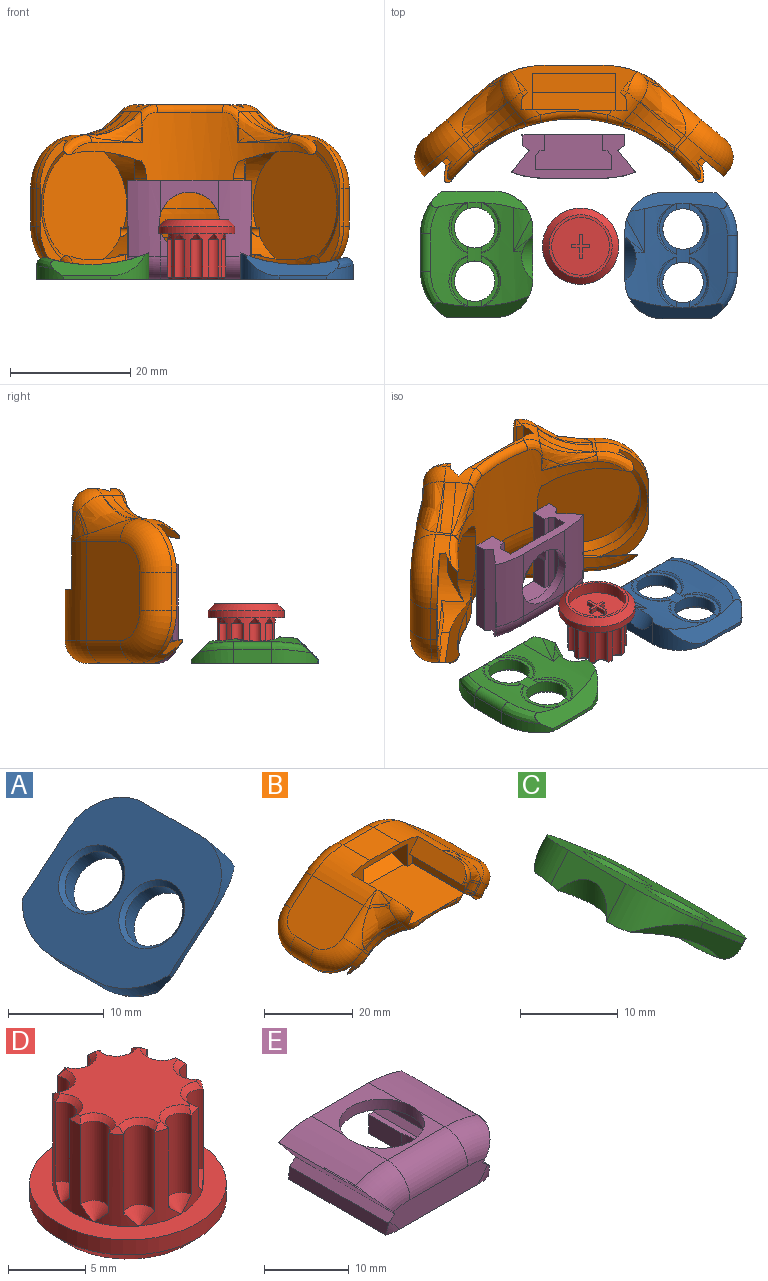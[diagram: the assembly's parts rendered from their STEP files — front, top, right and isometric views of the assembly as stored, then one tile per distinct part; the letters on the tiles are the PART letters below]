
ASSEMBLY  parts=5 mates=4
PART A: 33 faces, bbox 21.6x22.9x17.5 mm
  f0: torus R=39.28mm, axis (0,1,0), area 1.7mm2, adj f1,f2,f26,f30
  f1: cylinder r=25.31mm len=17.23mm, axis (0,1,0), area 130.5mm2, adj f0,f3,f4,f5,f7,f8,f9,f12
  f2: plane 8.4x3.45mm, normal (0.77,0,0.64), area 21.4mm2, adj f0,f23,f26,f28,f29,f30
  f3: cylinder r=1.27mm len=6.27mm, axis (0,1,0), area 14.9mm2, adj f1,f9,f11,f15
  f4: bspline ~8.68x3.45mm, area 3.7mm2, adj f1,f5,f25
  f5: plane 8.42x2.16mm, normal (0.64,0,-0.77), area 6.4mm2, adj f1,f4,f6,f13,f25
  f6: cylinder r=25.31mm len=1.74mm, axis (0,1,0), area 2.3mm2, adj f5,f7,f13,f25
  f7: plane 8.41x2.15mm, normal (0.64,0,-0.77), area 6.4mm2, adj f1,f6,f8,f13,f25
  f8: bspline ~8.68x3.09mm, area 3.7mm2, adj f1,f7,f25
  f9: bspline ~9.49x4.39mm, area 15.5mm2, adj f1,f3,f10,f25
  f10: cylinder r=8.89mm len=7.68mm, axis (0.64,0,-0.77), area 17.4mm2, adj f9,f11,f23,f24,f25
  f11: plane 6.27x1.82mm, normal (-0.77,0,-0.64), area 14.9mm2, adj f3,f10,f14,f23
  f12: cylinder r=3.37mm len=6.73mm, axis (0.64,0,-0.77), area 42.4mm2, adj f1,f17,f18,f19,f32
  f13: cylinder r=3.37mm len=6.73mm, axis (0.64,0,-0.77), area 42.4mm2, adj f1,f5,f6,f7,f31
  f14: cylinder r=8.89mm len=7.09mm, axis (0.64,0,-0.77), area 15.8mm2, adj f11,f15,f21,f22,f23
  f15: bspline ~9.03x3.89mm, area 13.3mm2, adj f1,f3,f14,f21
  f16: bspline ~8.68x3.09mm, area 3.7mm2, adj f1,f17,f21
  f17: plane 8.42x2.16mm, normal (0.64,0,-0.77), area 6.4mm2, adj f1,f12,f16,f18,f21
  f18: cylinder r=25.31mm len=1.74mm, axis (0,1,0), area 2.3mm2, adj f12,f17,f19,f21
  f19: plane 8.41x2.15mm, normal (0.64,0,-0.77), area 6.4mm2, adj f1,f12,f18,f20,f21
  f20: bspline ~8.68x3.45mm, area 3.7mm2, adj f1,f19,f21
  f21: plane 14.76x11.65mm, normal (0.45,0.71,-0.54), area 42.6mm2, adj f1,f14,f15,f16,f17,f18,f19,f20
  f22: plane 7.16x6.15mm, normal (0,1,0), area 5.5mm2, adj f14,f21,f23,f29
  f23: plane 21.03x14.32mm, normal (-0.64,0,0.77), area 264.2mm2, adj f2,f10,f11,f14,f22,f24,f28,f29
  f24: plane 6.48x5.58mm, normal (0,-1,0), area 4.9mm2, adj f10,f23,f25,f28
  f25: plane 15.01x11.45mm, normal (0.45,-0.71,-0.54), area 40.6mm2, adj f1,f4,f5,f6,f7,f8,f9,f10
  f26: bspline ~7.32x5.84mm, area 4.3mm2, adj f0,f2,f27,f29
  f27: cylinder r=13.97mm len=7.35mm, axis (0,1,0), area 12.5mm2, adj f1,f21,f26,f29
  f28: cylinder r=6.35mm len=7.7mm, axis (-0.64,0,0.77), area 25.5mm2, adj f1,f2,f23,f24,f25
  f29: cylinder r=6.35mm len=7.4mm, axis (0.64,0,-0.77), area 24.1mm2, adj f2,f21,f22,f23,f26,f27
  f30: cylinder r=4.57mm len=7.23mm, axis (0,0,-1), area 14.8mm2, adj f0,f1,f2
  f31: cone r=3.87mm half-angle=45deg, axis (-0.64,0,0.77), area 16.3mm2, adj f13,f23
  f32: cone r=3.87mm half-angle=45deg, axis (-0.64,0,0.77), area 16.3mm2, adj f12,f23
PART B: 137 faces, bbox 56.1x34.6x24.1 mm
  f0: plane 21.12x7.53mm, normal (0,-1,0), area 47.6mm2, adj f1,f2,f3,f99,f100,f101,f102,f103
  f1: cylinder r=15.24mm len=16.43mm, axis (0,1,0), area 128.4mm2, adj f0,f2,f10,f42,f77,f106
  f2: plane 9.64x8.55mm, normal (0,0,1), area 82.4mm2, adj f0,f1,f3,f76
  f3: cylinder r=15.24mm len=16.43mm, axis (0,1,0), area 128.4mm2, adj f0,f2,f41,f70,f74,f99
  f4: plane 12.68x0.82mm, normal (0,-1,0), area 4.9mm2, adj f7,f62,f72,f102
  f5: plane 1.14x0.86mm, normal (0,-1,0), area 0.5mm2, adj f7,f80,f105,f106
  f6: torus R=11.43mm, axis (0,-1,0), area 1.4mm2, adj f50,f75,f99
  f7: cylinder r=3.81mm len=5.54mm, axis (-0.64,0,-0.77), area 10.3mm2, adj f4,f5,f8,f78,f102,f103,f104,f105
  f8: sphere r=3.81mm, area 17.1mm2, adj f7,f9,f80,f106,f128,f129,f130
  f9: cylinder r=3.81mm len=3.91mm, axis (0,1,0), area 2.8mm2, adj f8,f106,f131
  f10: torus R=11.43mm, axis (0,1,0), area 3.6mm2, adj f1,f84,f106,f130,f131
  f11: cylinder r=25.31mm len=39.45mm, axis (0,1,0), area 308.2mm2, adj f13,f19,f24,f36,f38,f60,f61,f62
  f12: cylinder r=13.97mm len=4.51mm, axis (0,1,0), area 15.7mm2, adj f15,f25,f30,f45,f53,f96
  f13: torus R=39.28mm, axis (0,1,0), area 71.2mm2, adj f11,f15,f16,f43,f85,f86
  f14: cylinder r=13.97mm len=4.51mm, axis (0,1,0), area 15.7mm2, adj f16,f20,f29,f47,f58,f98
  f15: bspline ~7.09x5.93mm, area 4.8mm2, adj f12,f13,f45,f86,f96
  f16: bspline ~7.09x5.93mm, area 4.8mm2, adj f13,f14,f47,f85,f98
  f17: plane 21.59x6.29mm, normal (-0.64,0,-0.77), area 31.4mm2, adj f18,f21,f27,f32,f34,f133
  f18: plane 7.19x6.61mm, normal (0,1,0), area 9.2mm2, adj f17,f19,f34,f97,f133
  f19: plane 15.28x11.48mm, normal (0.45,0.71,0.54), area 38.4mm2, adj f11,f18,f34,f38,f97
  f20: plane 14.87x11.66mm, normal (0.45,-0.71,0.54), area 40.3mm2, adj f14,f21,f29,f32,f37,f98
  f21: plane 7.96x7.26mm, normal (0,-1,0), area 10.2mm2, adj f17,f20,f32,f98,f133
  f22: plane 21.59x6.29mm, normal (0.64,0,-0.77), area 31.4mm2, adj f23,f26,f28,f31,f33,f132
  f23: plane 7.19x6.61mm, normal (0,1,0), area 9.2mm2, adj f22,f24,f33,f95,f132
  f24: plane 15.28x11.48mm, normal (-0.45,0.71,0.54), area 38.4mm2, adj f11,f23,f33,f36,f95
  f25: plane 14.88x11.66mm, normal (-0.45,-0.71,0.54), area 40.3mm2, adj f12,f26,f30,f31,f35,f96
  f26: plane 7.96x7.26mm, normal (0,-1,0), area 10.2mm2, adj f22,f25,f31,f96,f132
  f27: plane 6.27x0.78mm, normal (0.77,0,-0.64), area 6.4mm2, adj f17,f32,f34,f82
  f28: plane 6.27x0.78mm, normal (-0.77,0,-0.64), area 6.4mm2, adj f22,f31,f33,f66
  f29: cylinder r=25.31mm len=9.36mm, axis (0,1,0), area 26mm2, adj f14,f20,f37,f59
  f30: cylinder r=25.31mm len=9.36mm, axis (0,1,0), area 26mm2, adj f12,f25,f35,f55
  f31: cylinder r=8.89mm len=8.89mm, axis (0.64,0,-0.77), area 24mm2, adj f22,f25,f26,f28,f35,f49,f68
  f32: cylinder r=8.89mm len=8.89mm, axis (0.64,0,0.77), area 24mm2, adj f17,f20,f21,f27,f37,f49,f81
  f33: cylinder r=8.89mm len=8.89mm, axis (0.64,0,-0.77), area 21.7mm2, adj f22,f23,f24,f28,f36,f40,f65
  f34: cylinder r=8.89mm len=8.89mm, axis (0.64,0,0.77), area 21.7mm2, adj f17,f18,f19,f27,f38,f39,f83
  f35: bspline ~7.63x7.4mm, area 14mm2, adj f25,f30,f31,f55
  f36: bspline ~7.2x7.09mm, area 13.2mm2, adj f11,f24,f33,f60
  f37: bspline ~7.97x7.63mm, area 14.1mm2, adj f20,f29,f32,f59
  f38: bspline ~7.63x7.4mm, area 13.2mm2, adj f11,f19,f34,f64
  f39: plane 2.3x2.04mm, normal (0,-1,0), area 1.4mm2, adj f34,f64,f84,f127,f128
  f40: plane 2.3x2.04mm, normal (0,-1,0), area 1.4mm2, adj f33,f60,f67,f119,f120
  f41: plane 16.43x10.53mm, normal (-0.64,0,0.77), area 214.6mm2, adj f3,f65,f66,f67,f68,f71
  f42: plane 16.43x10.53mm, normal (0.64,0,0.77), area 214.6mm2, adj f1,f79,f81,f82,f83,f84
  f43: cone r=29.12mm half-angle=20.6deg, axis (0,1,0), area 46.9mm2, adj f13,f44,f45,f47
  f44: torus R=15.15mm, axis (0,-1,0), area 3.3mm2, adj f43,f46,f48,f54
  f45: bspline ~10.91x6.7mm, area 21.1mm2, adj f12,f15,f43,f46,f51
  f46: bspline ~5.27x4.34mm, area 0.5mm2, adj f44,f45,f52
  f47: bspline ~9.02x6.04mm, area 21.1mm2, adj f14,f16,f43,f48,f57
  f48: bspline ~4.48x4.13mm, area 0.5mm2, adj f44,f47,f56
  f49: plane 37.6x10.17mm, normal (0,1,0), area 101.9mm2, adj f31,f32,f51,f52,f53,f54,f55,f56
  f50: plane 1.14x0.86mm, normal (0,-1,0), area 0.5mm2, adj f6,f72,f99,f100
  f51: bspline ~4.66x4.28mm, area 6mm2, adj f45,f49,f52,f53
  f52: bspline ~4.9x2.39mm, area 3mm2, adj f46,f49,f51,f54
  f53: torus R=12.7mm, axis (0,-1,0), area 10.6mm2, adj f12,f49,f51,f55
  f54: torus R=29.67mm, axis (0,-1,0), area 7.7mm2, adj f44,f49,f52,f56
  f55: torus R=26.58mm, axis (0,-1,0), area 13.5mm2, adj f30,f35,f49,f53
  f56: bspline ~5.22x2.59mm, area 3mm2, adj f48,f49,f54,f57
  f57: bspline ~4.76x4mm, area 6mm2, adj f47,f49,f56,f58
  f58: torus R=12.7mm, axis (0,-1,0), area 10.6mm2, adj f14,f49,f57,f59
  f59: torus R=26.58mm, axis (0,-1,0), area 13.5mm2, adj f29,f37,f49,f58
  f60: torus R=26.58mm, axis (0,1,0), area 4.1mm2, adj f11,f36,f40,f116,f117,f118
  f61: cylinder r=1.27mm len=2.54mm, axis (0,1,0), area 0.2mm2, adj f11,f69,f116
  f62: torus R=26.58mm, axis (0,-1,0), area 22.1mm2, adj f4,f11,f69,f78
  f63: cylinder r=1.27mm len=2.54mm, axis (0,1,0), area 0.2mm2, adj f11,f78,f124
  f64: torus R=26.58mm, axis (0,1,0), area 4.1mm2, adj f11,f38,f39,f124,f125,f126
  f65: torus R=5.08mm, axis (0.64,0,-0.77), area 70.6mm2, adj f33,f41,f66,f67
  f66: cylinder r=3.81mm len=6.27mm, axis (0,1,0), area 37.5mm2, adj f28,f41,f65,f68
  f67: cylinder r=3.81mm len=9.08mm, axis (-0.77,0,-0.64), area 26.4mm2, adj f40,f41,f65,f70,f121
  f68: torus R=5.08mm, axis (0.64,0,-0.77), area 70.6mm2, adj f31,f41,f66,f71
  f69: bspline ~4.53x4.24mm, area 5.8mm2, adj f11,f61,f62,f72,f117
  f70: torus R=11.43mm, axis (0,1,0), area 3.6mm2, adj f3,f67,f99,f122,f123
  f71: cylinder r=3.81mm len=9.08mm, axis (-0.77,0,-0.64), area 51.8mm2, adj f41,f49,f68,f74
  f72: cylinder r=3.81mm len=5.54mm, axis (-0.64,0,0.77), area 10.5mm2, adj f4,f50,f69,f75,f100,f101,f102,f118
  f73: cylinder r=3.81mm len=3.91mm, axis (0,1,0), area 2.8mm2, adj f75,f99,f123
  f74: torus R=11.43mm, axis (0,-1,0), area 57.9mm2, adj f3,f49,f71,f76
  f75: sphere r=3.81mm, area 17.1mm2, adj f6,f72,f73,f99,f120,f121,f122
  f76: cylinder r=3.81mm len=9.64mm, axis (1,0,0), area 57.7mm2, adj f2,f49,f74,f77
  f77: torus R=11.43mm, axis (0,-1,0), area 57.9mm2, adj f1,f49,f76,f79
  f78: bspline ~4.67x4.6mm, area 5.8mm2, adj f7,f11,f62,f63,f125
  f79: cylinder r=3.81mm len=9.08mm, axis (-0.77,0,0.64), area 51.8mm2, adj f42,f49,f77,f81
  f80: torus R=11.43mm, axis (0,-1,0), area 1.4mm2, adj f5,f8,f106
  f81: torus R=5.08mm, axis (-0.64,0,-0.77), area 70.6mm2, adj f32,f42,f79,f82
  f82: cylinder r=3.81mm len=6.27mm, axis (0,-1,0), area 37.5mm2, adj f27,f42,f81,f83
  f83: torus R=5.08mm, axis (-0.64,0,-0.77), area 70.6mm2, adj f34,f42,f82,f84
  f84: cylinder r=3.81mm len=9.08mm, axis (-0.77,0,0.64), area 26.4mm2, adj f10,f39,f42,f83,f129
  f85: plane 8.96x2.27mm, normal (0.77,0,-0.64), area 24.8mm2, adj f11,f13,f16,f97,f98,f135
  f86: plane 8.96x2.42mm, normal (-0.77,0,-0.64), area 26.4mm2, adj f11,f13,f15,f93,f95,f96
  f87: plane 20.61x15.79mm, normal (0.64,0,-0.77), area 332.1mm2, adj f89,f114,f115
  f88: plane 8.92x0.78mm, normal (-0.64,0,0.77), area 6.1mm2, adj f89,f93
  f89: cylinder r=10.29mm len=20.57mm, axis (0.64,0,-0.77), area 205.3mm2, adj f87,f88,f93,f95,f96,f114,f115,f132
  f90: plane 20.61x15.79mm, normal (-0.64,0,-0.77), area 332.1mm2, adj f92,f112,f113
  f91: plane 8.92x0.78mm, normal (0.64,0,0.77), area 6.1mm2, adj f92,f94
  f92: cylinder r=10.29mm len=20.57mm, axis (-0.64,0,-0.77), area 205.5mm2, adj f90,f91,f94,f97,f98,f112,f113,f133
  f93: plane 16.79x4.71mm, normal (-1,0,0.09), area 31.9mm2, adj f86,f88,f89,f95,f96
  f94: plane 15.48x3.51mm, normal (1,0,0.09), area 28.6mm2, adj f91,f92,f134,f135,f136
  f95: cylinder r=6.35mm len=8.47mm, axis (0.64,0,-0.77), area 23.7mm2, adj f11,f23,f24,f86,f89,f93,f132
  f96: cylinder r=6.35mm len=8.11mm, axis (-0.64,0,0.77), area 21.9mm2, adj f12,f15,f25,f26,f86,f89,f93,f132
  f97: cylinder r=6.35mm len=8.47mm, axis (-0.64,0,-0.77), area 22.8mm2, adj f11,f18,f19,f85,f92,f133,f134
  f98: cylinder r=6.35mm len=8.11mm, axis (0.64,0,0.77), area 21mm2, adj f14,f16,f20,f21,f85,f92,f133,f136
  f99: plane 17.07x3.73mm, normal (0.77,0,0.64), area 71.6mm2, adj f0,f3,f6,f50,f70,f73,f75,f100
  f100: plane 16.76x0.95mm, normal (0.64,0,-0.77), area 20.8mm2, adj f0,f50,f72,f99,f101
  f101: plane 16.8x2.17mm, normal (1,0,-0.09), area 35.2mm2, adj f0,f72,f100,f102
  f102: plane 17.97x17.47mm, normal (0,0,1), area 306.2mm2, adj f0,f4,f7,f72,f101,f103,f108,f109
  f103: plane 16.34x0.23mm, normal (0,0,1), area 3.7mm2, adj f0,f7,f102,f104
  f104: plane 16.8x2.24mm, normal (-1,0,-0.09), area 36.4mm2, adj f0,f7,f103,f105
  f105: plane 16.76x0.95mm, normal (-0.64,0,-0.77), area 20.8mm2, adj f0,f5,f7,f104,f106
  f106: plane 17.07x3.73mm, normal (-0.77,0,0.64), area 71.6mm2, adj f0,f1,f5,f8,f9,f10,f80,f105
  f107: plane 13.97x8.89mm, normal (0,0,-1), area 124.2mm2, adj f0,f108,f109,f110
  f108: plane 8.89x6.05mm, normal (1,0,0), area 40.8mm2, adj f0,f102,f107,f110,f111,f115
  f109: plane 8.89x6.11mm, normal (-1,0,0), area 40.9mm2, adj f0,f102,f107,f110,f111,f112
  f110: plane 13.97x3.18mm, normal (0,-1,0), area 44.4mm2, adj f107,f108,f109,f111
  f111: plane 13.97x7.9mm, normal (0,-0.35,0.94), area 116.6mm2, adj f102,f108,f109,f110
  f112: cylinder r=0.76mm len=4.52mm, axis (1,0,0), area 19.4mm2, adj f90,f92,f109,f113
  f113: plane 1.5x0.7mm, normal (-1,0,0), area 0.6mm2, adj f90,f92,f112
  f114: plane 1.5x0.7mm, normal (1,0,0), area 0.6mm2, adj f87,f89,f115
  f115: cylinder r=0.76mm len=4.52mm, axis (1,0,0), area 19mm2, adj f87,f89,f108,f114
  f116: bspline ~3.88x3.08mm, area 2.9mm2, adj f60,f61,f117
  f117: bspline ~8.81x5.26mm, area 17.9mm2, adj f60,f69,f116,f118
  f118: bspline ~8.64x7.23mm, area 11.5mm2, adj f60,f72,f117,f119
  f119: cylinder r=12.7mm len=8.22mm, axis (-0.64,0,0.77), area 19.1mm2, adj f40,f72,f118,f120
  f120: torus R=11.91mm, axis (0,1,0), area 4mm2, adj f40,f75,f119,f121
  f121: bspline ~10.27x8.1mm, area 46.5mm2, adj f67,f75,f120,f122
  f122: bspline ~4.59x3.59mm, area 2.7mm2, adj f70,f75,f121,f123
  f123: bspline ~6.84x4.86mm, area 9.7mm2, adj f70,f73,f99,f122
  f124: bspline ~3.88x3.08mm, area 2.9mm2, adj f63,f64,f125
  f125: bspline ~8.81x5.25mm, area 17.9mm2, adj f64,f78,f124,f126
  f126: bspline ~9.14x7.9mm, area 11.5mm2, adj f7,f64,f125,f127
  f127: cylinder r=12.7mm len=8.22mm, axis (-0.64,0,-0.77), area 19.1mm2, adj f7,f39,f126,f128
  f128: torus R=11.91mm, axis (0,1,0), area 4mm2, adj f8,f39,f127,f129
  f129: bspline ~10.27x8.1mm, area 46.5mm2, adj f8,f84,f128,f130
  f130: bspline ~4.59x3.59mm, area 2.7mm2, adj f8,f10,f129,f131
  f131: bspline ~6.12x4.41mm, area 9.7mm2, adj f9,f10,f106,f130
  f132: cone r=11.3mm half-angle=53.1deg, axis (0.64,0,-0.77), area 47.6mm2, adj f22,f23,f26,f89,f95,f96
  f133: cone r=11.3mm half-angle=53.1deg, axis (-0.64,0,-0.77), area 47.6mm2, adj f17,f18,f21,f92,f97,f98
  f134: bspline ~3.93x2.04mm, area 1.5mm2, adj f92,f94,f97,f135
  f135: cylinder r=0.46mm len=8.89mm, axis (0,1,0), area 3.2mm2, adj f85,f94,f134,f136
  f136: bspline ~3.93x2.04mm, area 1.5mm2, adj f92,f94,f98,f135
PART C: 33 faces, bbox 20.3x23x17.5 mm
  f0: torus R=39.28mm, axis (0,1,0), area 1.7mm2, adj f1,f20,f27,f30
  f1: cylinder r=25.31mm len=17.23mm, axis (0,1,0), area 130.5mm2, adj f0,f2,f3,f4,f5,f7,f8,f11
  f2: cylinder r=1.27mm len=6.27mm, axis (0,1,0), area 14.9mm2, adj f1,f3,f9,f18
  f3: bspline ~9.84x4.82mm, area 15.5mm2, adj f1,f2,f10,f25
  f4: bspline ~8.68x3.09mm, area 3.7mm2, adj f1,f5,f25
  f5: plane 8.42x2.16mm, normal (-0.64,0,-0.77), area 6.4mm2, adj f1,f4,f6,f12,f25
  f6: cylinder r=25.31mm len=1.74mm, axis (0,1,0), area 2.3mm2, adj f5,f7,f12,f25
  f7: plane 8.41x2.15mm, normal (-0.64,0,-0.77), area 6.4mm2, adj f1,f6,f8,f12,f25
  f8: bspline ~8.68x3.45mm, area 3.7mm2, adj f1,f7,f25
  f9: plane 6.27x1.82mm, normal (0.77,0,-0.64), area 14.9mm2, adj f2,f10,f19,f23
  f10: cylinder r=8.89mm len=7.68mm, axis (0.64,0,0.77), area 17.4mm2, adj f3,f9,f23,f24,f25
  f11: cylinder r=3.37mm len=6.73mm, axis (-0.64,0,-0.77), area 42.4mm2, adj f1,f14,f15,f16,f31
  f12: cylinder r=3.37mm len=6.73mm, axis (-0.64,0,-0.77), area 42.4mm2, adj f1,f5,f6,f7,f32
  f13: bspline ~8.68x3.45mm, area 3.7mm2, adj f1,f14,f21
  f14: plane 8.42x2.16mm, normal (-0.64,0,-0.77), area 6.4mm2, adj f1,f11,f13,f15,f21
  f15: cylinder r=25.31mm len=1.74mm, axis (0,1,0), area 2.3mm2, adj f11,f14,f16,f21
  f16: plane 8.41x2.15mm, normal (-0.64,0,-0.77), area 6.4mm2, adj f1,f11,f15,f17,f21
  f17: bspline ~8.68x3.09mm, area 3.7mm2, adj f1,f16,f21
  f18: bspline ~8.6x3.51mm, area 13.3mm2, adj f1,f2,f19,f21
  f19: cylinder r=8.89mm len=7.09mm, axis (0.64,0,0.77), area 15.8mm2, adj f9,f18,f21,f22,f23
  f20: bspline ~5.57x4.46mm, area 4.3mm2, adj f0,f26,f27,f29
  f21: plane 14.77x11.65mm, normal (-0.45,0.71,-0.54), area 42.6mm2, adj f1,f13,f14,f15,f16,f17,f18,f19
  f22: plane 7.16x6.15mm, normal (0,1,0), area 5.5mm2, adj f19,f21,f23,f29
  f23: plane 21.03x14.32mm, normal (0.64,0,0.77), area 264.2mm2, adj f9,f10,f19,f22,f24,f27,f28,f29
  f24: plane 6.48x5.58mm, normal (0,-1,0), area 4.9mm2, adj f10,f23,f25,f28
  f25: plane 15.01x11.45mm, normal (-0.45,-0.71,-0.54), area 40.6mm2, adj f1,f3,f4,f5,f6,f7,f8,f10
  f26: cylinder r=13.97mm len=7.35mm, axis (0,1,0), area 12.5mm2, adj f1,f20,f21,f29
  f27: plane 8.4x3.45mm, normal (-0.77,0,0.64), area 21.4mm2, adj f0,f20,f23,f28,f29,f30
  f28: cylinder r=6.35mm len=7.7mm, axis (-0.64,0,-0.77), area 25.5mm2, adj f1,f23,f24,f25,f27
  f29: cylinder r=6.35mm len=7.4mm, axis (0.64,0,0.77), area 24.1mm2, adj f20,f21,f22,f23,f26,f27
  f30: cylinder r=4.57mm len=7.23mm, axis (0,0,-1), area 14.8mm2, adj f0,f1,f27
  f31: cone r=3.87mm half-angle=45deg, axis (0.64,0,0.77), area 16.3mm2, adj f11,f23
  f32: cone r=3.87mm half-angle=45deg, axis (0.64,0,0.77), area 16.3mm2, adj f12,f23
PART D: 70 faces, bbox 12.7x12.7x9.9 mm
  f0: plane 9.6x9.6mm, normal (0,0,-1), area 69.2mm2, adj f24,f36,f37,f38,f39,f40,f41,f42
  f1: cylinder r=1.02mm len=6.27mm, axis (0,0,-1), area 18.7mm2, adj f2,f20,f33,f68
  f2: cylinder r=4.85mm len=7.24mm, axis (0,0,-1), area 8.3mm2, adj f1,f3,f22,f32,f33,f66
  f3: cylinder r=1.02mm len=6.27mm, axis (0,0,-1), area 18.7mm2, adj f2,f4,f32,f64
  f4: cylinder r=4.85mm len=7.24mm, axis (0,0,-1), area 8.3mm2, adj f3,f5,f22,f31,f32,f62
  f5: cylinder r=1.02mm len=6.27mm, axis (0,0,-1), area 18.7mm2, adj f4,f6,f31,f60
  f6: cylinder r=4.85mm len=7.24mm, axis (0,0,-1), area 8.3mm2, adj f5,f7,f22,f30,f31,f58
  f7: cylinder r=1.02mm len=6.27mm, axis (0,0,-1), area 18.7mm2, adj f6,f8,f30,f56
  f8: cylinder r=4.85mm len=7.24mm, axis (0,0,-1), area 8.3mm2, adj f7,f9,f22,f29,f30,f54
  f9: cylinder r=1.02mm len=6.27mm, axis (0,0,-1), area 18.7mm2, adj f8,f10,f29,f52
  f10: cylinder r=4.85mm len=7.24mm, axis (0,0,-1), area 8.3mm2, adj f9,f11,f22,f28,f29,f50
  f11: cylinder r=1.02mm len=6.27mm, axis (0,0,-1), area 18.7mm2, adj f10,f12,f28,f49
  f12: cylinder r=4.85mm len=7.24mm, axis (0,0,-1), area 8.3mm2, adj f11,f13,f22,f27,f28,f51
  f13: cylinder r=1.02mm len=6.27mm, axis (0,0,-1), area 18.7mm2, adj f12,f14,f27,f53
  f14: cylinder r=4.85mm len=7.24mm, axis (0,0,-1), area 8.3mm2, adj f13,f15,f22,f26,f27,f55
  f15: cylinder r=1.02mm len=6.27mm, axis (0,0,-1), area 18.7mm2, adj f14,f16,f26,f57
  f16: cylinder r=4.85mm len=7.24mm, axis (0,0,-1), area 8.3mm2, adj f15,f17,f22,f26,f35,f59
  f17: cylinder r=1.02mm len=6.27mm, axis (0,0,-1), area 18.7mm2, adj f16,f18,f35,f61
  f18: cylinder r=4.85mm len=7.24mm, axis (0,0,-1), area 8.3mm2, adj f17,f19,f22,f34,f35,f63
  f19: cylinder r=1.02mm len=6.27mm, axis (0,0,-1), area 18.7mm2, adj f18,f20,f34,f65
  f20: cylinder r=4.85mm len=7.24mm, axis (0,0,-1), area 8.3mm2, adj f1,f19,f22,f33,f34,f67
  f21: plane 8.94x8.57mm, normal (0,0,1), area 44.3mm2, adj f49,f50,f51,f52,f53,f54,f55,f56
  f22: plane 12.7x12.7mm, normal (0,0,1), area 52.8mm2, adj f2,f4,f6,f8,f10,f12,f14,f16
  f23: cylinder r=6.35mm len=12.7mm, axis (0,0,1), area 47.6mm2, adj f22,f69
  f24: cylinder r=4.8mm len=9.6mm, axis (0,0,1), area 61.3mm2, adj f0,f25
  f25: plane 10.52x10.52mm, normal (0,0,-1), area 14.4mm2, adj f24,f69
  f26: cone r=0.05mm half-angle=45deg, axis (0,0,1), area 2.2mm2, adj f14,f15,f16,f22
  f27: cone r=0.05mm half-angle=45deg, axis (0,0,1), area 2.2mm2, adj f12,f13,f14,f22
  f28: cone r=0.05mm half-angle=45deg, axis (0,0,1), area 2.2mm2, adj f10,f11,f12,f22
  f29: cone r=0.05mm half-angle=45deg, axis (0,0,1), area 2.2mm2, adj f8,f9,f10,f22
  f30: cone r=0.05mm half-angle=45deg, axis (0,0,1), area 2.2mm2, adj f6,f7,f8,f22
  f31: cone r=0.05mm half-angle=45deg, axis (0,0,1), area 2.2mm2, adj f4,f5,f6,f22
  f32: cone r=0.05mm half-angle=45deg, axis (0,0,1), area 2.2mm2, adj f2,f3,f4,f22
  f33: cone r=0.05mm half-angle=45deg, axis (0,0,1), area 2.2mm2, adj f1,f2,f20,f22
  f34: cone r=0.05mm half-angle=45deg, axis (0,0,1), area 2.2mm2, adj f18,f19,f20,f22
  f35: cone r=0.05mm half-angle=45deg, axis (0,0,1), area 2.2mm2, adj f16,f17,f18,f22
  f36: plane 0.76x0.51mm, normal (0,-1,0), area 0.4mm2, adj f0,f37,f47,f48
  f37: plane 1.73x0.76mm, normal (-1,0,0), area 1.3mm2, adj f0,f36,f38,f48
  f38: plane 1.21x0.76mm, normal (0,-1,0), area 0.9mm2, adj f0,f37,f39,f48
  f39: plane 0.76x0.51mm, normal (-1,0,0), area 0.4mm2, adj f0,f38,f40,f48
  f40: plane 1.21x0.76mm, normal (0,1,0), area 0.9mm2, adj f0,f39,f41,f48
  f41: plane 1.73x0.76mm, normal (-1,0,0), area 1.3mm2, adj f0,f40,f42,f48
  f42: plane 0.76x0.51mm, normal (0,1,0), area 0.4mm2, adj f0,f41,f43,f48
  f43: plane 1.73x0.76mm, normal (1,0,0), area 1.3mm2, adj f0,f42,f44,f48
  f44: plane 1.21x0.76mm, normal (0,1,0), area 0.9mm2, adj f0,f43,f45,f48
  f45: plane 0.76x0.51mm, normal (1,0,0), area 0.4mm2, adj f0,f44,f46,f48
  f46: plane 1.21x0.76mm, normal (0,-1,0), area 0.9mm2, adj f0,f45,f47,f48
  f47: plane 1.73x0.76mm, normal (1,0,0), area 1.3mm2, adj f0,f36,f46,f48
  f48: plane 3.96x2.92mm, normal (0,0,-1), area 3.2mm2, adj f36,f37,f38,f39,f40,f41,f42,f43
  f49: cone r=1.02mm half-angle=45deg, axis (0,0,1), area 1.7mm2, adj f11,f21,f50,f51
  f50: cone r=4.47mm half-angle=45deg, axis (0,0,-1), area 0.3mm2, adj f10,f21,f49,f52
  f51: cone r=4.47mm half-angle=45deg, axis (0,0,-1), area 0.3mm2, adj f12,f21,f49,f53
  f52: cone r=1.02mm half-angle=45deg, axis (0,0,1), area 1.7mm2, adj f9,f21,f50,f54
  f53: cone r=1.02mm half-angle=45deg, axis (0,0,1), area 1.7mm2, adj f13,f21,f51,f55
  f54: cone r=4.47mm half-angle=45deg, axis (0,0,-1), area 0.3mm2, adj f8,f21,f52,f56
  f55: cone r=4.47mm half-angle=45deg, axis (0,0,-1), area 0.3mm2, adj f14,f21,f53,f57
  f56: cone r=1.02mm half-angle=45deg, axis (0,0,1), area 1.7mm2, adj f7,f21,f54,f58
  f57: cone r=1.02mm half-angle=45deg, axis (0,0,1), area 1.7mm2, adj f15,f21,f55,f59
  f58: cone r=4.47mm half-angle=45deg, axis (0,0,-1), area 0.3mm2, adj f6,f21,f56,f60
  f59: cone r=4.47mm half-angle=45deg, axis (0,0,-1), area 0.3mm2, adj f16,f21,f57,f61
  f60: cone r=1.02mm half-angle=45deg, axis (0,0,1), area 1.7mm2, adj f5,f21,f58,f62
  f61: cone r=1.02mm half-angle=45deg, axis (0,0,1), area 1.7mm2, adj f17,f21,f59,f63
  f62: cone r=4.47mm half-angle=45deg, axis (0,0,-1), area 0.3mm2, adj f4,f21,f60,f64
  f63: cone r=4.47mm half-angle=45deg, axis (0,0,-1), area 0.3mm2, adj f18,f21,f61,f65
  f64: cone r=1.02mm half-angle=45deg, axis (0,0,1), area 1.7mm2, adj f3,f21,f62,f66
  f65: cone r=1.02mm half-angle=45deg, axis (0,0,1), area 1.7mm2, adj f19,f21,f63,f67
  f66: cone r=4.47mm half-angle=45deg, axis (0,0,-1), area 0.3mm2, adj f2,f21,f64,f68
  f67: cone r=4.47mm half-angle=45deg, axis (0,0,-1), area 0.3mm2, adj f20,f21,f65,f68
  f68: cone r=1.02mm half-angle=45deg, axis (0,0,1), area 1.7mm2, adj f1,f21,f66,f67
  f69: cone r=5.26mm half-angle=45deg, axis (0,0,1), area 56.3mm2, adj f23,f25
PART E: 39 faces, bbox 22.2x16.5x8.6 mm
  f0: plane 9.64x5.59mm, normal (0,0,1), area 28.2mm2, adj f20,f22,f25,f34
  f1: plane 5.53x2.72mm, normal (-1,0,0), area 15mm2, adj f3,f26,f33,f36
  f2: plane 5.53x2.68mm, normal (1,0,0), area 14.8mm2, adj f3,f29,f33,f35
  f3: plane 17.18x16.54mm, normal (0,0,-1), area 147.7mm2, adj f1,f2,f9,f10,f15,f23,f24,f25
  f4: cylinder r=3.81mm len=9.64mm, axis (1,0,0), area 57.7mm2, adj f5,f14,f15,f21
  f5: torus R=11.43mm, axis (0,-1,0), area 27.6mm2, adj f4,f6,f15,f17,f22
  f6: sphere r=3.81mm, area 0.2mm2, adj f5,f7,f17
  f7: cylinder r=3.81mm len=5.08mm, axis (0,1,0), area 0.9mm2, adj f6,f8,f17,f22
  f8: torus R=11.43mm, axis (0,1,0), area 0mm2, adj f7,f17,f22
  f9: cylinder r=3.81mm len=3.04mm, axis (-0.64,0,-0.77), area 2.3mm2, adj f3,f15,f16,f24
  f10: cylinder r=3.81mm len=2.95mm, axis (-0.64,0,0.77), area 2.2mm2, adj f3,f15,f19,f23
  f11: torus R=11.43mm, axis (0,1,0), area 0mm2, adj f12,f18,f20
  f12: cylinder r=3.81mm len=5.08mm, axis (0,1,0), area 0.9mm2, adj f11,f13,f18,f20
  f13: sphere r=3.81mm, area 0.2mm2, adj f12,f14,f18
  f14: torus R=11.43mm, axis (0,-1,0), area 27.6mm2, adj f4,f13,f15,f18,f20
  f15: plane 16.41x3.49mm, normal (0,-1,0), area 51.2mm2, adj f3,f4,f5,f9,f10,f14,f16,f17
  f16: plane 16.51x1.05mm, normal (0.64,0,0.77), area 22.7mm2, adj f9,f15,f17,f24,f25
  f17: plane 16.51x3.54mm, normal (0.77,0,-0.64), area 73mm2, adj f5,f6,f7,f8,f15,f16,f22,f25
  f18: plane 16.51x3.54mm, normal (-0.77,0,-0.64), area 73mm2, adj f11,f12,f13,f14,f15,f19,f20,f25
  f19: plane 16.51x1.05mm, normal (-0.64,0,0.77), area 22.7mm2, adj f10,f15,f18,f23,f25
  f20: cylinder r=15.24mm len=12.7mm, axis (0,1,0), area 70.4mm2, adj f0,f11,f12,f14,f18,f21,f25,f34
  f21: plane 9.64x4.32mm, normal (0,0,1), area 15.9mm2, adj f4,f20,f22,f34
  f22: cylinder r=15.24mm len=12.7mm, axis (0,1,0), area 70.4mm2, adj f0,f5,f7,f8,f17,f21,f25,f34
  f23: plane 16.53x1.8mm, normal (-1,0,0.09), area 29.2mm2, adj f3,f10,f19,f25
  f24: plane 16.53x1.88mm, normal (1,0,0.09), area 30.3mm2, adj f3,f9,f16,f25
  f25: plane 20.67x7.3mm, normal (0,1,0), area 61mm2, adj f0,f3,f16,f17,f18,f19,f20,f22
  f26: plane 13.97x0.79mm, normal (0,0,1), area 10.6mm2, adj f1,f25,f27,f33,f36,f38
  f27: plane 5.53x2.72mm, normal (-1,0,0), area 15mm2, adj f3,f25,f26,f36
  f28: plane 5.53x2.68mm, normal (1,0,0), area 14.8mm2, adj f3,f25,f29,f35
  f29: plane 13.97x0.79mm, normal (0,0,1), area 10.6mm2, adj f2,f25,f28,f33,f35,f37
  f30: plane 13.97x2.29mm, normal (1,0,0), area 31.9mm2, adj f25,f31,f33,f37
  f31: plane 13.97x12.7mm, normal (0,0,-1), area 98.4mm2, adj f25,f30,f32,f33,f34
  f32: plane 13.97x2.29mm, normal (-1,0,0), area 31.9mm2, adj f25,f31,f33,f38
  f33: plane 12.7x5.76mm, normal (0,1,0), area 64mm2, adj f1,f2,f3,f26,f29,f30,f31,f32
  f34: cylinder r=5.02mm len=10.03mm, axis (0,0,-1), area 48mm2, adj f0,f20,f21,f22,f31
  f35: cylinder r=5.02mm len=2.91mm, axis (0,0,-1), area 7.9mm2, adj f2,f3,f28,f29
  f36: cylinder r=5.02mm len=2.91mm, axis (0,0,-1), area 8mm2, adj f1,f3,f26,f27
  f37: plane 13.97x0.76mm, normal (0.71,0,0.71), area 15.1mm2, adj f25,f29,f30,f33
  f38: plane 13.97x0.76mm, normal (-0.71,0,0.71), area 15.1mm2, adj f25,f26,f32,f33
PLACE A rot(axis=(0,-1,0),140deg) t=(26.19,-4.82,30.91)mm
PLACE B rot(axis=(-1,0,0),90deg) t=(8.03,7.66,30.46)mm fixed
PLACE C rot(axis=(0,1,0),140deg) t=(-8.49,-4.62,30.91)mm
PLACE D rot(axis=(1,0,0),180deg) t=(9.14,11.77,10.73)mm
PLACE E rot(axis=(1,0,0),90deg) t=(7.95,57.33,4.89)mm
MATE planar B.f49 <-> A.f23  axis (0,0,-1) through (8.03,33.87,3.11)mm
MATE planar A.f23 <-> C.f23  axis (0,0,-1) through (35.21,10.51,3.11)mm
MATE planar E.f15 <-> A.f23  axis (0,0,-1) through (7.92,30.34,3.11)mm
MATE planar D.f6 <-> C.f23  axis (0,0,-1) through (9.14,11.77,3.11)mm
